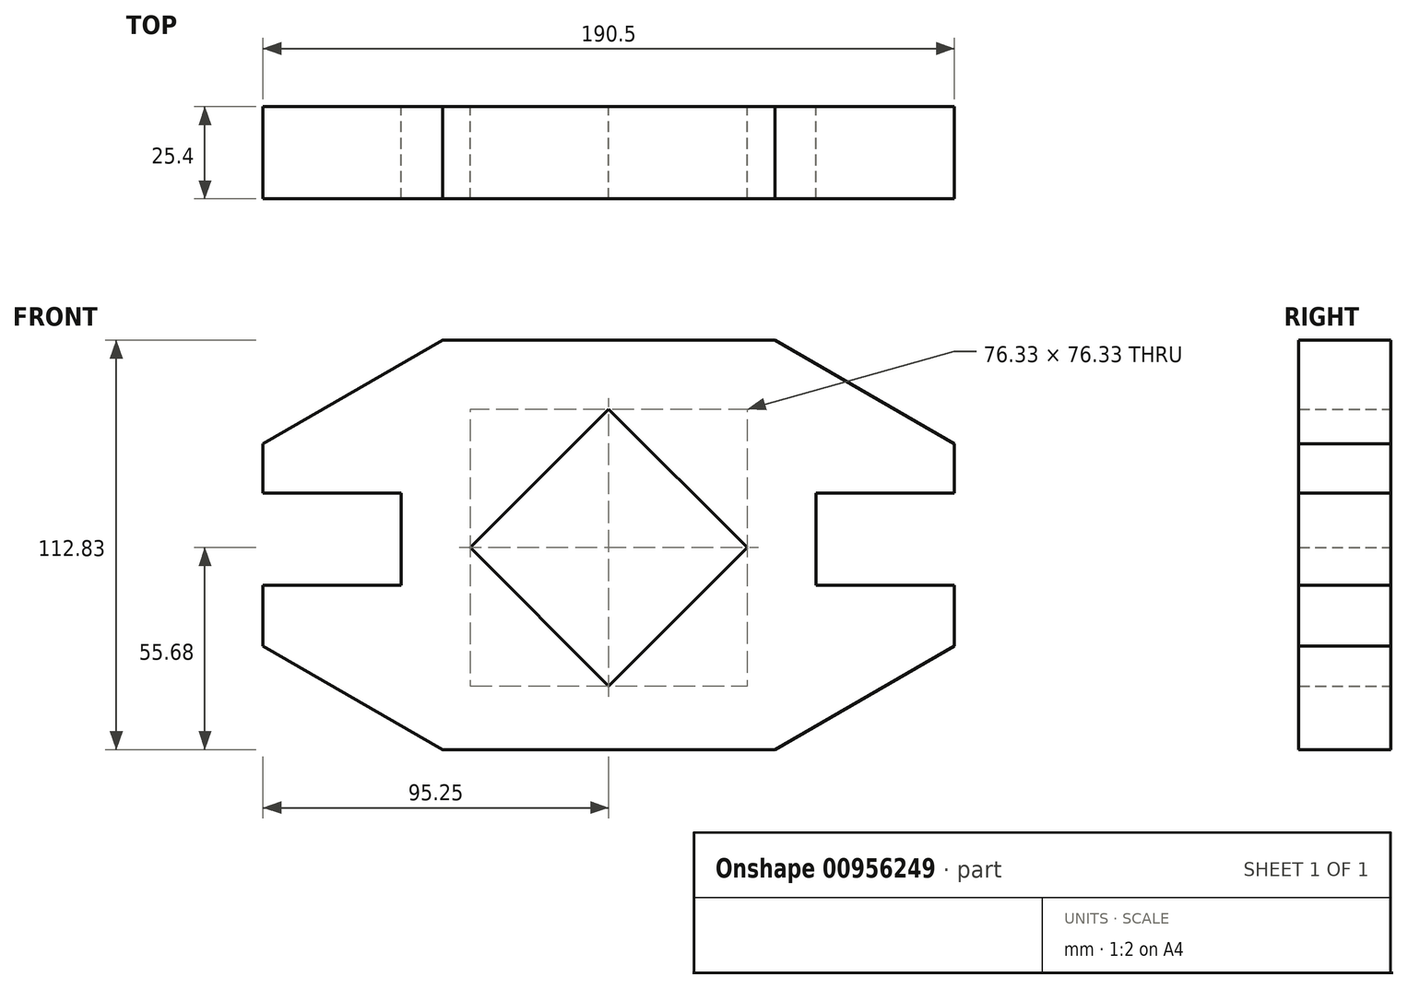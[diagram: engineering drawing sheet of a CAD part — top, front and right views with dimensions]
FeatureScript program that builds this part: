
annotation { "Feature Type Name" : "Feature", "Feature Type Description" : "" }
export const myFeature = defineFeature(function(context is Context, id is Id, definition is map)
    precondition{}
    {
        {
            var Q0;
            Q0=qCreatedBy(makeId("Front.planeOp"),FACE);
            var sketch = newSketch(context, id + "F0", { "sketchPlane" : qUnion([Q0])});
            skLineSegment(sketch, "E0", {"start": v(0, 38.17) * mm, "end": v(38.17, 0) * mm});
            skLineSegment(sketch, "E1.MirrorCS", {"start": v(0, 38.17) * mm, "end": v(-38.17, 0) * mm});
            skLineSegment(sketch, "E2.MirrorCS", {"start": v(0, -38.17) * mm, "end": v(-38.17, 0) * mm});
            skLineSegment(sketch, "E3.MirrorCS", {"start": v(0, -38.17) * mm, "end": v(38.17, 0) * mm});
            skLineSegment(sketch, "E4.bottom", {"start": v(-45.76, 57.15) * mm, "end": v(45.76, 57.15) * mm});
            skLineSegment(sketch, "E4.top", {"start": v(-45.76, -55.68) * mm, "end": v(45.76, -55.68) * mm});
            skLineSegment(sketch, "E4.left", {"start": v(-95.25, 28.57) * mm, "end": v(-95.25, 15.02) * mm});
            skLineSegment(sketch, "E4.right", {"start": v(95.25, 28.57) * mm, "end": v(95.25, 15.02) * mm});
            skPoint(sketch, "E4.middle", {"position": v(0, 0) * mm});
            skLineSegment(sketch, "E5", {"start": v(45.76, 57.15) * mm, "end": v(95.25, 28.57) * mm});
            skLineSegment(sketch, "E6.MirrorCS", {"start": v(-45.76, 57.15) * mm, "end": v(-95.25, 28.57) * mm});
            skLineSegment(sketch, "E7", {"start": v(-57.15, 0.73) * mm, "end": v(57.15, 0.73) * mm});
            skLineSegment(sketch, "E8.MirrorCS", {"start": v(45.76, -55.68) * mm, "end": v(95.25, -27.1) * mm});
            skLineSegment(sketch, "E9.MirrorCS", {"start": v(-45.76, -55.68) * mm, "end": v(-95.25, -27.1) * mm});
            skPoint(sketch, "E10.MirrorCS.end.orphan", {"position": v(-95.25, 28.57) * mm});
            skLineSegment(sketch, "E11", {"start": v(95.25, -10.38) * mm, "end": v(95.25, -27.1) * mm});
            skLineSegment(sketch, "E12", {"start": v(0, 57.15) * mm, "end": v(95.25, 57.15) * mm});
            skLineSegment(sketch, "E13", {"start": v(95.25, 15.02) * mm, "end": v(57.15, 15.02) * mm});
            skLineSegment(sketch, "E14", {"start": v(57.15, 15.02) * mm, "end": v(57.15, -10.38) * mm});
            skLineSegment(sketch, "E15", {"start": v(57.15, -10.38) * mm, "end": v(95.25, -10.38) * mm});
            skLineSegment(sketch, "E16.MirrorCS", {"start": v(-95.25, 15.02) * mm, "end": v(-57.15, 15.02) * mm});
            skLineSegment(sketch, "E17.MirrorCS", {"start": v(-57.15, 15.02) * mm, "end": v(-57.15, -10.38) * mm});
            skLineSegment(sketch, "E18.MirrorCS", {"start": v(-57.15, -10.38) * mm, "end": v(-95.25, -10.38) * mm});
            skLineSegment(sketch, "E19.trimOffspring", {"start": v(-95.25, -10.38) * mm, "end": v(-95.25, -27.1) * mm});
            skLineSegment(sketch, "E20", {"start": v(111.6, 0) * mm, "end": v(111.6, -57.15) * mm});
            skSolve(sketch);
        }
        {
            var Q0;
            Q0 = qSketchRegion(id + "F0", true);
            extrude(context, id + "F1", {"entities" : qUnion([Q0]), "depth" : 25.4 * mm, "offsetDistance" : 25.4 * mm});
        }
    });
